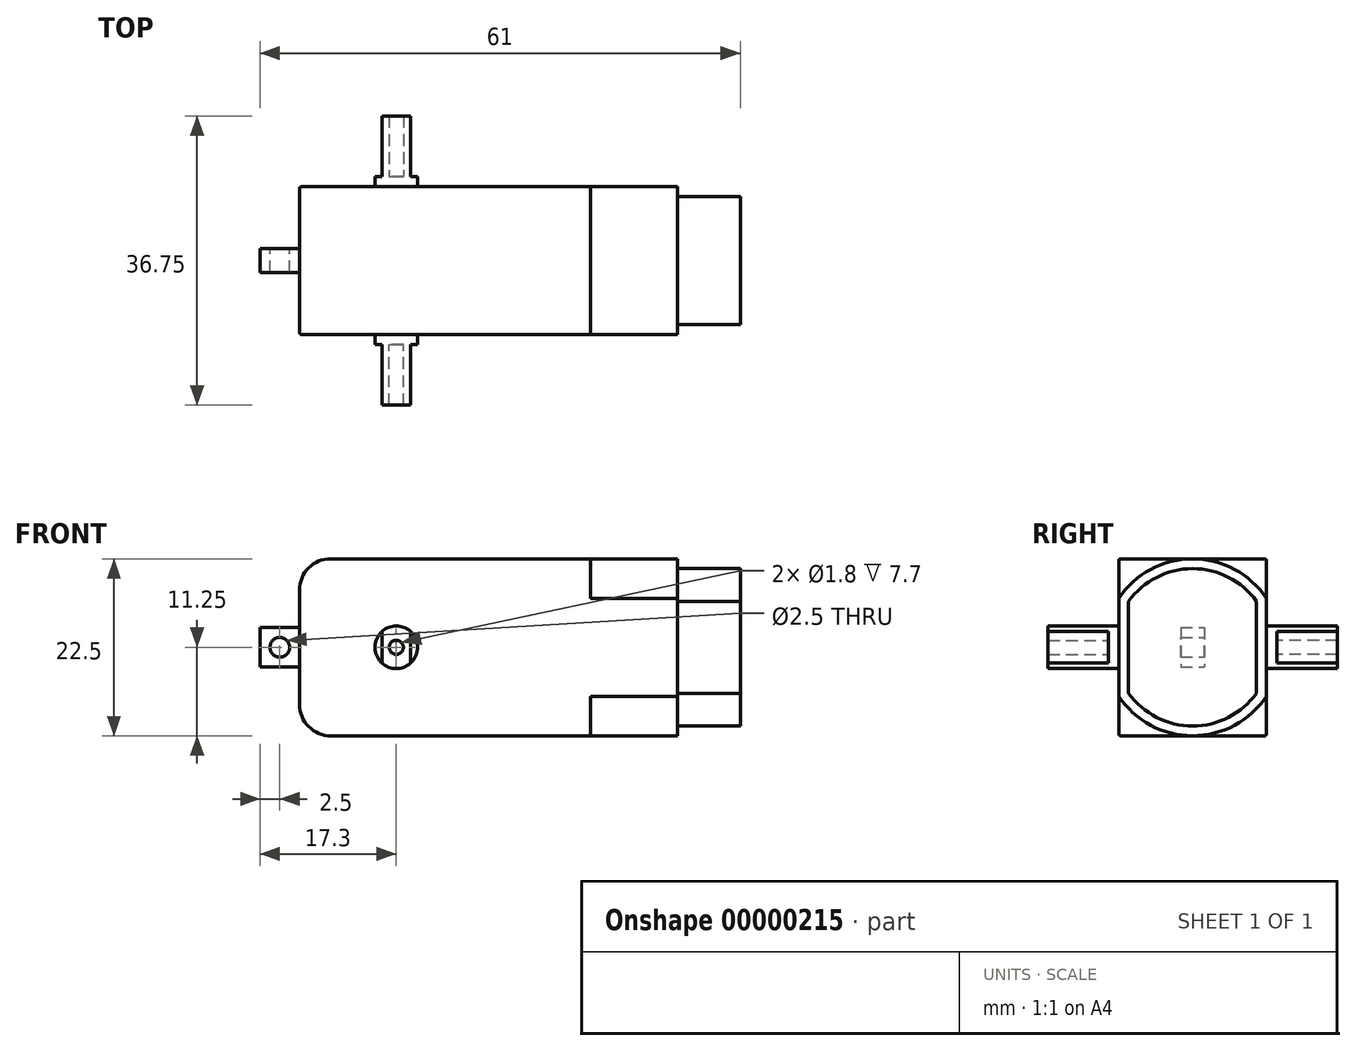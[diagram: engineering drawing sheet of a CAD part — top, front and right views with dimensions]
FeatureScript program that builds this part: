
annotation { "Feature Type Name" : "Feature", "Feature Type Description" : "" }
export const myFeature = defineFeature(function(context is Context, id is Id, definition is map)
    precondition{}
    {
        {
            var Q0;
            Q0=qCreatedBy(makeId("Front.planeOp"),FACE);
            var sketch = newSketch(context, id + "F0", { "sketchPlane" : qUnion([Q0])});
            skCircle(sketch, "E0", {"center": v(0, 0) * mm, "radius": 2.7 * mm});
            skLineSegment(sketch, "E1", {"start": v(-1.8, 2.01) * mm, "end": v(-1.8, -2.01) * mm});
            skLineSegment(sketch, "E2", {"start": v(0, 0) * mm, "end": v(0, 2.7) * mm});
            skLineSegment(sketch, "E3.0.MirrorCS", {"start": v(1.8, 2.01) * mm, "end": v(1.8, -2.01) * mm});
            skCircle(sketch, "E4", {"center": v(0, 0) * mm, "radius": 0.9 * mm});
            skSolve(sketch);
        }
        {
            var Q0;
            {var subQ0=sQuery(id+"F0.wireOp",EDGE,"E1");var subQ1=makeQuery(id+"F0.imprint","IMPRINT",EDGE,{"derivedFrom":subQ0});var subQ5=sQuery(id+"F0.wireOp",EDGE,"E3.0.MirrorCS");var subQ6=makeQuery(id+"F0.imprint","IMPRINT",EDGE,{"derivedFrom":subQ5});var subQ9=sQuery(id+"F0.wireOp",EDGE,"E4");var subQ10=makeQuery(id+"F0.imprint","IMPRINT",EDGE,{"derivedFrom":subQ9});Q0=qUnion([makeQuery(id+"F0.imprint","IMPRINT",FACE,{"disambiguationData":[TD([[subQ1,-1.0]])]}),makeQuery(id+"F0.imprint","IMPRINT",FACE,{"disambiguationData":[TD([[subQ6,1.0]])]}),makeQuery(id+"F0.imprint","IMPRINT",FACE,{"disambiguationData":[TD([[subQ10,1.0]])]}),makeQuery(id+"F0.imprint","IMPRINT",FACE,{"disambiguationData":[TD([[subQ1,1.0]])]})]);}
            extrude(context, id + "F1", {"entities" : qUnion([Q0]), "depth" : 1.3 * mm});
        }
        {
            var Q0;
            {var subQ2=sQuery(id+"F0.wireOp",EDGE,"E1");Q0=makeQuery(id+"F0.imprint","IMPRINT",FACE,{"disambiguationData":[TD([[makeQuery(id+"F0.imprint","IMPRINT",EDGE,{"derivedFrom":subQ2}),1.0]])]});}
            extrude(context, id + "F2", {"entities" : qUnion([Q0]), "operationType" : NewBodyOperationType.ADD, "depth" : 9 * mm});
        }
        {
            var Q0;
            Q0=qCreatedBy(makeId("Front.planeOp"),FACE);
            var sketch = newSketch(context, id + "F3", { "sketchPlane" : qUnion([Q0])});
            skLineSegment(sketch, "E5.bottom", {"start": v(-8.3, 11.25) * mm, "end": v(24.7, 11.25) * mm});
            skLineSegment(sketch, "E5.top", {"start": v(-8.3, -11.25) * mm, "end": v(24.7, -11.25) * mm});
            skLineSegment(sketch, "E5.left", {"start": v(-12.3, 7.25) * mm, "end": v(-12.3, -7.25) * mm});
            skLineSegment(sketch, "E5.right", {"start": v(24.7, 11.25) * mm, "end": v(24.7, -11.25) * mm});
            skLineSegment(sketch, "E6", {"start": v(-12.3, 0) * mm, "end": v(24.7, 0) * mm, "construction": true});
            skPoint(sketch, "E7.visualSharp", {"position": v(-12.3, 11.25) * mm});
            skArc(sketch, "E7.filletArc", {"start": v(-8.3, 11.25) * mm, "mid": v(-11.13, 10.08) * mm, "end": v(-12.3, 7.25) * mm});
            skPoint(sketch, "E8.visualSharp", {"position": v(-12.3, -11.25) * mm});
            skArc(sketch, "E8.filletArc", {"start": v(-12.3, -7.25) * mm, "mid": v(-11.13, -10.08) * mm, "end": v(-8.3, -11.25) * mm});
            skSolve(sketch);
        }
        {
            var Q0;
            Q0=makeQuery(id+"F3.imprint","IMPRINT",FACE,{"disambiguationData":[TD([[makeQuery(id+"F3.imprint","IMPRINT",EDGE,{"derivedFrom":sQuery(id+"F3.wireOp",EDGE,"E5.bottom")}),-1.0]])]});
            extrude(context, id + "F4", {"entities" : qUnion([Q0]), "oppositeDirection" : true, "depth" : 18.75 * mm});
        }
        {
            var Q0;
            Q0=makeQuery(id+"F4.opExtrude","CAP_FACE",FACE,{"disambiguationData":[OSD([sQuery(id+"F3.wireOp",EDGE,"E5.bottom"),sQuery(id+"F3.wireOp",EDGE,"E5.top"),sQuery(id+"F3.wireOp",EDGE,"E5.left"),sQuery(id+"F3.wireOp",EDGE,"E5.right"),sQuery(id+"F3.wireOp",EDGE,"E7.filletArc"),sQuery(id+"F3.wireOp",EDGE,"E8.filletArc")])],"isStart":true});
            cPlane(context, id + "F5", {"entities" : qUnion([Q0]), "cplaneType" : CPlaneType.OFFSET, "offset" : 9.38 * mm, "oppositeDirection" : true, "width" : 150 * mm, "height" : 150 * mm});
        }
        {
            var Q0;
            Q0=makeQuery(id+"F1.opExtrude","SWEPT_BODY",BODY,{"disambiguationData":[OSD([sQuery(id+"F0.wireOp",EDGE,"E0")])]});
            var Q1;
            Q1=qCreatedBy(id+"F5.planeOp",FACE);
            mirror(context, id + "F6", {"entities" : qUnion([Q0]), "mirrorPlane" : qUnion([Q1])});
        }
        {
            var Q0;
            Q0=qCreatedBy(id+"F5.planeOp",FACE);
            var sketch = newSketch(context, id + "F7", { "sketchPlane" : qUnion([Q0])});
            skLineSegment(sketch, "E9.bottom", {"start": v(-17.3, 2.5) * mm, "end": v(-12.3, 2.5) * mm});
            skLineSegment(sketch, "E9.top", {"start": v(-17.3, -2.5) * mm, "end": v(-12.3, -2.5) * mm});
            skLineSegment(sketch, "E9.left", {"start": v(-17.3, 2.5) * mm, "end": v(-17.3, -2.5) * mm});
            skLineSegment(sketch, "E9.right", {"start": v(-12.3, 2.5) * mm, "end": v(-12.3, -2.5) * mm});
            skLineSegment(sketch, "E10", {"start": v(-17.3, 0) * mm, "end": v(-12.3, 0) * mm, "construction": true});
            skCircle(sketch, "E11", {"center": v(-14.8, 0) * mm, "radius": 1.25 * mm});
            skSolve(sketch);
        }
        {
            var Q0;
            Q0=makeQuery(id+"F7.imprint","IMPRINT",FACE,{"disambiguationData":[TD([[makeQuery(id+"F7.imprint","IMPRINT",EDGE,{"derivedFrom":sQuery(id+"F7.wireOp",EDGE,"E9.bottom")}),-1.0]])]});
            extrude(context, id + "F8", {"entities" : qUnion([Q0]), "operationType" : NewBodyOperationType.ADD, "endBound" : BoundingType.SYMMETRIC, "depth" : 3 * mm});
        }
        {
            var Q0;
            Q0=makeQuery(id+"F4.opExtrude","SWEPT_FACE",FACE,{"disambiguationData":[OSD([sQuery(id+"F3.wireOp",EDGE,"E5.right")])]});
            var sketch = newSketch(context, id + "F9", { "sketchPlane" : qUnion([Q0])});
            skLineSegment(sketch, "E12", {"start": v(0, 11.25) * mm, "end": v(18.75, -11.25) * mm, "construction": true});
            skCircle(sketch, "E13", {"center": v(9.38, 0) * mm, "radius": 11.25 * mm});
            skLineSegment(sketch, "E14.0", {"start": v(0, 11.25) * mm, "end": v(0, -11.25) * mm});
            skLineSegment(sketch, "E14.1", {"start": v(18.75, 11.25) * mm, "end": v(18.75, -11.25) * mm});
            skSolve(sketch);
        }
        {
            var Q0;
            Q0=makeQuery(id+"F4.opExtrude","CAP_EDGE",EDGE,{"disambiguationData":[OSD([sQuery(id+"F3.wireOp",EDGE,"E5.bottom")])],"isStart":true});
            var Q1;
            Q1=makeQuery(id+"F4.opExtrude","CAP_EDGE",EDGE,{"disambiguationData":[OSD([sQuery(id+"F3.wireOp",EDGE,"E5.bottom")])],"isStart":false});
            fillet(context, id + "F10", {"entities" : qUnion([Q0, Q1]), "radius" : 0.25 * mm, "tangentPropagation" : true, "allowEdgeOverflow" : false});
        }
        {
            var Q0;
            {var subQ1=sQuery(id+"F9.wireOp",EDGE,"E13");var subQ4=sQuery(id+"F9.wireOp",EDGE,"E14.0");var subQ6=makeQuery(id+"F9.imprint","INTERSECT",VERTEX,{"disambiguationData":[OD(0.0)],"derivedFrom":[subQ1,subQ4]});Q0=makeQuery(id+"F9.imprint","IMPRINT",FACE,{"disambiguationData":[TD([[makeQuery(id+"F9.imprint","IMPRINT",EDGE,{"disambiguationData":[TD([[subQ6,-1.0]])],"derivedFrom":subQ4}),1.0]])]});}
            extrude(context, id + "F11", {"entities" : qUnion([Q0]), "operationType" : NewBodyOperationType.ADD, "depth" : 11 * mm});
        }
        {
            var Q0;
            Q0=makeQuery(id+"F11.opExtrude","CAP_FACE",FACE,{"disambiguationData":[OSD([sQuery(id+"F9.wireOp",EDGE,"E13"),sQuery(id+"F9.wireOp",EDGE,"E14.0"),sQuery(id+"F9.wireOp",EDGE,"E14.1")])],"isStart":false});
            var sketch = newSketch(context, id + "F12", { "sketchPlane" : qUnion([Q0])});
            skArc(sketch, "E15.0", {"start": v(17.5, 5.83) * mm, "mid": v(9.38, 10) * mm, "end": v(1.25, 5.83) * mm});
            skLineSegment(sketch, "E15.1", {"start": v(17.5, 5.83) * mm, "end": v(17.5, -5.83) * mm});
            skArc(sketch, "E15.2", {"start": v(1.25, -5.83) * mm, "mid": v(9.38, -10) * mm, "end": v(17.5, -5.83) * mm});
            skLineSegment(sketch, "E15.3", {"start": v(1.25, 5.83) * mm, "end": v(1.25, -5.83) * mm});
            skSolve(sketch);
        }
        {
            var Q0;
            Q0=makeQuery(id+"F12.imprint","IMPRINT",FACE,{"disambiguationData":[TD([[makeQuery(id+"F12.imprint","IMPRINT",EDGE,{"derivedFrom":sQuery(id+"F12.wireOp",EDGE,"E15.0")}),1.0]])]});
            extrude(context, id + "F13", {"entities" : qUnion([Q0]), "depth" : 8 * mm});
        }
    });
